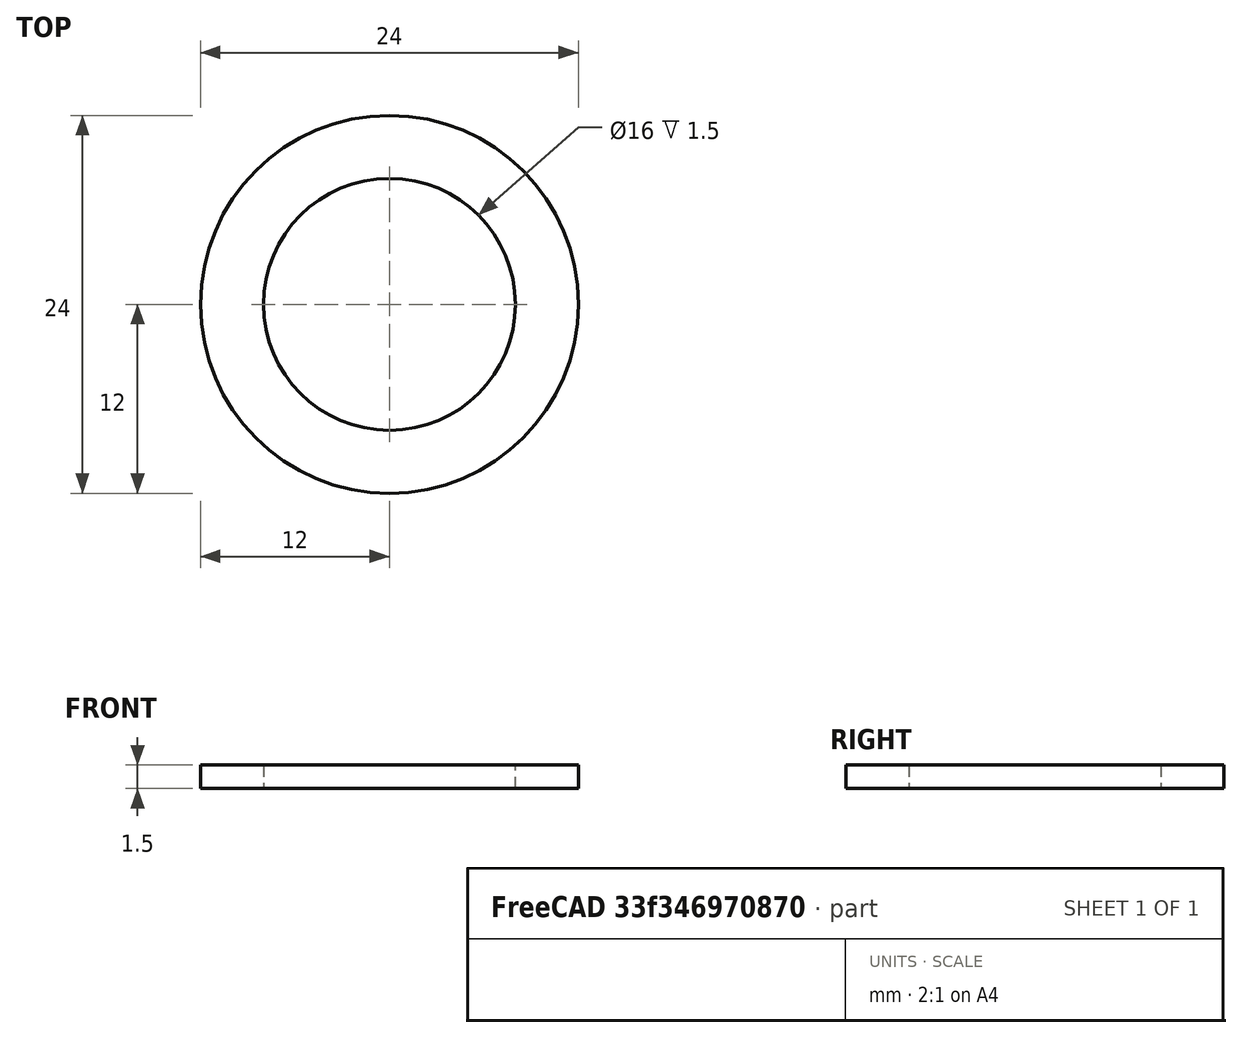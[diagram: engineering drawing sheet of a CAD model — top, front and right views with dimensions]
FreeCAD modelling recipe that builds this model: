
FCSTD DOCUMENT  (FreeCAD 0.19R24276 (Git))
Label: roller_16x20_edge
License: All rights reserved
LicenseURL: http://en.wikipedia.org/wiki/All_rights_reserved
objects: Sketcher::SketchObject×1, PartDesign::Pad×1, PartDesign::Body×1
note: 4 computed .brp shape members not serialized (recipe doc carries the construction recipe); baked Part::Feature solids carry a one-line shape summary decoded from their .brp

FEATURE [Sketcher::SketchObject] Sketch
  FullyConstrained = true
  MapMode = 5
  Support = -> [XY_Plane]
  sketch-geometry (2):
    g0: Circle CenterX=0 CenterY=0 CenterZ=0 NormalX=0 NormalY=0 NormalZ=1 AngleXU=0 Radius=8
    g1: Circle CenterX=0 CenterY=0 CenterZ=0 NormalX=0 NormalY=0 NormalZ=1 AngleXU=0 Radius=12
  constraints (4):
    c: Coincident(g0,g-1)
    c: Coincident(g1,g0)
    c: Diameter(g0) = 16
    c: Diameter(g1) = 24
FEATURE [PartDesign::Pad] Pad
  Direction = (1,1,1)
  Length = 1.5
  Length2 = 100
  Profile = -> Sketch
  Type = 0
FEATURE [PartDesign::Body] Body
  Group = -> [Sketch,Pad]
  Origin = -> Origin
  Tip = -> Pad
